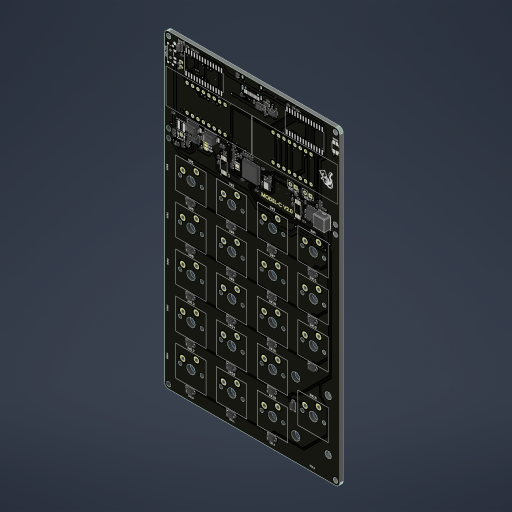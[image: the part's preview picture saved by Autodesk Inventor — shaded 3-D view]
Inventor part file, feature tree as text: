
AUTODESK INVENTOR PART (.ipt)
format: ipt  version: 2024.2 (Build 282272000, 272)  size: 3,942,400 bytes
history: native  units: mm
features: other x5, sketch x2
ambient origin geometry x8: Origin, YZ Plane, XZ Plane, XY Plane, X Axis, Y Axis, Z Axis, Center Point
bodies: Solid1 (feature_tree), Solid2 (feature_tree), Solid3 (feature_tree), Solid4 (feature_tree), Solid5 (feature_tree), Solid6 (feature_tree), Solid7 (feature_tree), Solid8 (feature_tree), Solid9 (feature_tree), Solid10 (feature_tree), Solid11 (feature_tree), Solid12 (feature_tree), Solid13 (feature_tree), Solid14 (feature_tree), Solid15 (feature_tree), Solid16 (feature_tree), Solid17 (feature_tree), Solid18 (feature_tree), Solid19 (feature_tree), Solid20 (feature_tree), Solid21 (feature_tree), Solid22 (feature_tree), Solid23 (feature_tree), Solid24 (feature_tree), Solid25 (feature_tree), Solid26 (feature_tree), Solid27 (feature_tree), Solid28 (feature_tree), Solid29 (feature_tree), Solid30 (feature_tree), Solid31 (feature_tree), Solid32 (feature_tree), Solid33 (feature_tree), Solid34 (feature_tree), Solid36 (feature_tree), Solid37 (feature_tree), Solid38 (feature_tree), Solid39 (feature_tree), Solid40 (feature_tree), Solid41 (feature_tree), Solid42 (feature_tree), Solid43 (feature_tree), Solid44 (feature_tree), Solid45 (feature_tree), Solid46 (feature_tree), Solid48 (feature_tree), Solid49 (feature_tree), Solid50 (feature_tree), Solid51 (feature_tree), Solid52 (feature_tree), Solid53 (feature_tree), Solid54 (feature_tree), Solid55 (feature_tree), Solid56 (feature_tree), Solid57 (feature_tree), Solid58 (feature_tree), Solid59 (feature_tree), Solid60 (feature_tree), Solid61 (feature_tree), Solid62 (feature_tree), Solid63 (feature_tree), Solid64 (feature_tree), Solid65 (feature_tree), Solid66 (feature_tree), Solid67 (feature_tree), Solid68 (feature_tree), Solid69 (feature_tree), Solid70 (feature_tree), Solid71 (feature_tree), Solid72 (feature_tree), Solid73 (feature_tree), Solid74 (feature_tree), Solid75 (feature_tree), Solid76 (feature_tree), Solid77 (feature_tree), Solid78 (feature_tree), Solid79 (feature_tree), Solid80 (feature_tree), Solid81 (feature_tree), Solid82 (feature_tree), Solid83 (feature_tree), Solid84 (feature_tree), Solid85 (feature_tree), Solid86 (feature_tree), Solid87 (feature_tree), Solid88 (feature_tree), Solid89 (feature_tree), Solid90 (feature_tree), Solid91 (feature_tree), Solid92 (feature_tree), Solid93 (feature_tree), Solid94 (feature_tree), Solid95 (feature_tree), Solid96 (feature_tree), Solid97 (feature_tree), Solid98 (feature_tree), Solid99 (feature_tree), Solid100 (feature_tree), Solid101 (feature_tree), Solid102 (feature_tree), Solid103 (feature_tree), Solid104 (feature_tree), Solid105 (feature_tree), Solid106 (feature_tree), Solid107 (feature_tree), Solid108 (feature_tree), Solid109 (feature_tree), Solid110 (feature_tree), Solid111 (feature_tree), Solid112 (feature_tree)
feature tree (7):
  other  "Decal1"
  other  "Decal2"
  sketch  "Sketch1"
  other  "Image1"
  sketch  "Sketch2"
  other  "Image2"
  other  "Finish1"
